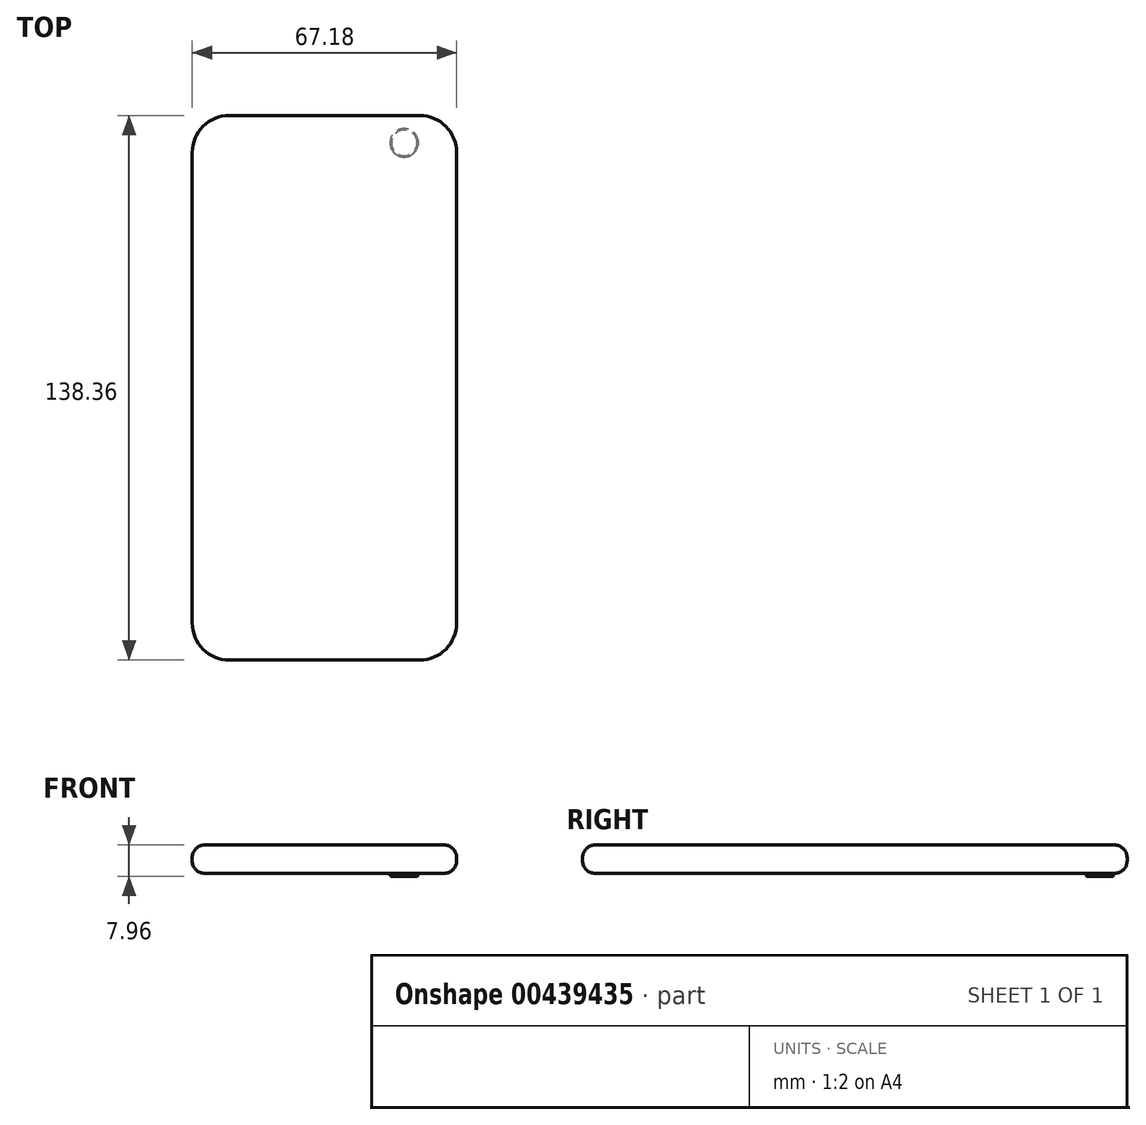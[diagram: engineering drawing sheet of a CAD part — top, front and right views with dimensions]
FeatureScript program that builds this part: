
annotation { "Feature Type Name" : "Feature", "Feature Type Description" : "" }
export const myFeature = defineFeature(function(context is Context, id is Id, definition is map)
    precondition{}
    {
        {
            var Q0;
            Q0=qCreatedBy(makeId("Top.planeOp"),FACE);
            var sketch = newSketch(context, id + "F0", { "sketchPlane" : qUnion([Q0])});
            skLineSegment(sketch, "E0.bottom", {"start": v(-33.59, 69.18) * mm, "end": v(33.6, 69.18) * mm});
            skLineSegment(sketch, "E0.top", {"start": v(-33.6, -69.17) * mm, "end": v(33.59, -69.17) * mm});
            skLineSegment(sketch, "E0.left", {"start": v(-33.59, 69.18) * mm, "end": v(-33.6, -69.17) * mm});
            skLineSegment(sketch, "E0.right", {"start": v(33.6, 69.17) * mm, "end": v(33.59, -69.18) * mm});
            skPoint(sketch, "E0.middle", {"position": v(0, 0) * mm});
            skSolve(sketch);
        }
        {
            var Q0;
            Q0 = qSketchRegion(id + "F0", true);
            extrude(context, id + "F1", {"entities" : qUnion([Q0]), "depth" : 7.2 * mm});
        }
        {
            var Q0;
            Q0=makeQuery(id+"F1.opExtrude","SWEPT_EDGE",EDGE,{"disambiguationData":[OSD([sQuery(id+"F0.wireOp",EDGE,"E0.bottom"),sQuery(id+"F0.wireOp",EDGE,"E0.right")])]});
            var Q1;
            Q1=makeQuery(id+"F1.opExtrude","SWEPT_EDGE",EDGE,{"disambiguationData":[OSD([sQuery(id+"F0.wireOp",EDGE,"E0.bottom"),sQuery(id+"F0.wireOp",EDGE,"E0.left")])]});
            var Q2;
            Q2=makeQuery(id+"F1.opExtrude","SWEPT_EDGE",EDGE,{"disambiguationData":[OSD([sQuery(id+"F0.wireOp",EDGE,"E0.top"),sQuery(id+"F0.wireOp",EDGE,"E0.left")])]});
            var Q3;
            Q3=makeQuery(id+"F1.opExtrude","SWEPT_EDGE",EDGE,{"disambiguationData":[OSD([sQuery(id+"F0.wireOp",EDGE,"E0.top"),sQuery(id+"F0.wireOp",EDGE,"E0.right")])]});
            fillet(context, id + "F2", {"entities" : qUnion([Q0, Q1, Q2, Q3]), "radius" : 9.4 * mm, "tangentPropagation" : true, "allowEdgeOverflow" : false});
        }
        {
            var Q0;
            Q0=makeQuery(id+"F1.opExtrude","CAP_EDGE",EDGE,{"disambiguationData":[OSD([sQuery(id+"F0.wireOp",EDGE,"E0.right")])],"isStart":true});
            var Q1;
            Q1=makeQuery(id+"F1.opExtrude","CAP_EDGE",EDGE,{"disambiguationData":[OSD([sQuery(id+"F0.wireOp",EDGE,"E0.right")])],"isStart":false});
            fillet(context, id + "F3", {"entities" : qUnion([Q0, Q1]), "radius" : 3.2 * mm, "tangentPropagation" : true, "allowEdgeOverflow" : false});
        }
        {
            var Q0;
            Q0=makeQuery(id+"F1.opExtrude","CAP_FACE",FACE,{"disambiguationData":[OSD([sQuery(id+"F0.wireOp",EDGE,"E0.bottom"),sQuery(id+"F0.wireOp",EDGE,"E0.top"),sQuery(id+"F0.wireOp",EDGE,"E0.left"),sQuery(id+"F0.wireOp",EDGE,"E0.right")])],"isStart":true});
            var sketch = newSketch(context, id + "F4", { "sketchPlane" : qUnion([Q0])});
            skCircle(sketch, "E1", {"center": v(20.27, -62.24) * mm, "radius": 3.6 * mm});
            skLineSegment(sketch, "E2", {"start": v(24.2, -69.18) * mm, "end": v(-24.19, -69.18) * mm, "construction": true});
            skLineSegment(sketch, "E3", {"start": v(33.59, 59.77) * mm, "end": v(33.6, -59.78) * mm, "construction": true});
            skSolve(sketch);
        }
        {
            var Q0;
            Q0 = qSketchRegion(id + "F4", true);
            extrude(context, id + "F5", {"entities" : qUnion([Q0]), "operationType" : NewBodyOperationType.ADD, "depth" : .76 * mm});
        }
        {
            var Q0;
            Q0=makeQuery(id+"F5.opExtrude","CAP_EDGE",EDGE,{"disambiguationData":[OSD([sQuery(id+"F4.wireOp",EDGE,"E1")])],"isStart":false});
            chamfer(context, id + "F6", {"entities" : qUnion([Q0]), "width" : .33 * mm, "tangentPropagation" : true});
        }
    });
